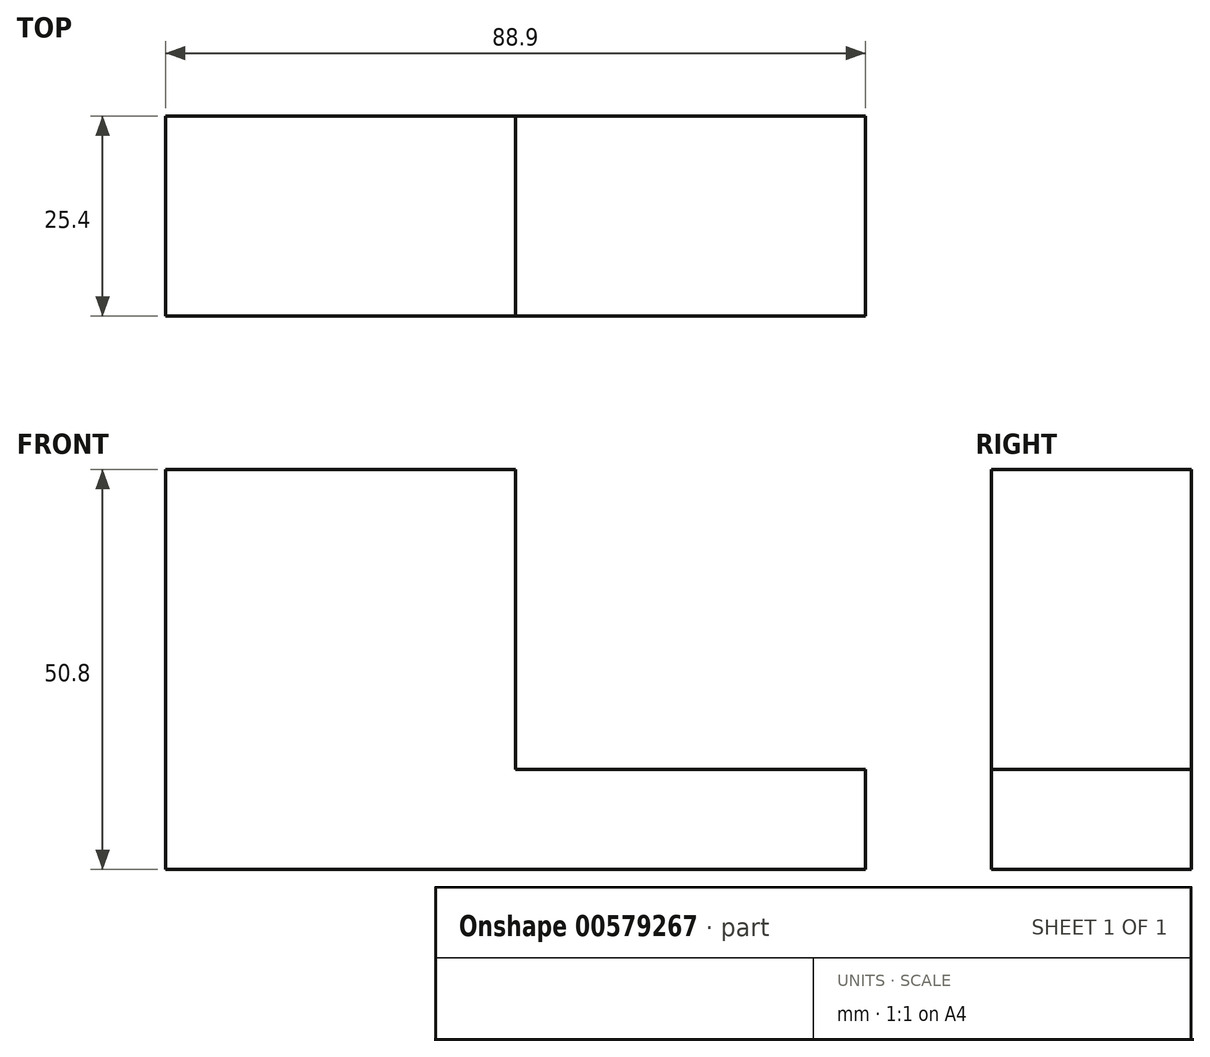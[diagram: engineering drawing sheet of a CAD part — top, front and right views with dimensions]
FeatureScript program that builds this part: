
annotation { "Feature Type Name" : "Feature", "Feature Type Description" : "" }
export const myFeature = defineFeature(function(context is Context, id is Id, definition is map)
    precondition{}
    {
        {
            var Q0;
            Q0=qCreatedBy(makeId("Front.planeOp"),FACE);
            var sketch = newSketch(context, id + "F0", { "sketchPlane" : qUnion([Q0])});
            skLineSegment(sketch, "E0", {"start": v(-48.67, 0) * mm, "end": v(40.23, 0) * mm});
            skLineSegment(sketch, "E1", {"start": v(40.23, 0) * mm, "end": v(40.23, 12.7) * mm});
            skLineSegment(sketch, "E2", {"start": v(40.23, 12.7) * mm, "end": v(-4.22, 12.7) * mm});
            skLineSegment(sketch, "E3", {"start": v(-4.22, 12.7) * mm, "end": v(-4.22, 50.8) * mm});
            skLineSegment(sketch, "E4", {"start": v(-4.22, 50.8) * mm, "end": v(-48.67, 50.8) * mm});
            skLineSegment(sketch, "E5", {"start": v(-48.67, 50.8) * mm, "end": v(-48.67, 0) * mm});
            skSolve(sketch);
        }
        {
            var Q0;
            Q0=makeQuery(id+"F0.imprint","IMPRINT",FACE,{"disambiguationData":[TD([[makeQuery(id+"F0.imprint","IMPRINT",EDGE,{"derivedFrom":sQuery(id+"F0.wireOp",EDGE,"E0")}),1.0]])]});
            extrude(context, id + "F1", {"entities" : qUnion([Q0]), "depth" : 25.4 * mm, "offsetDistance" : 25.4 * mm});
        }
        {
            var Q0;
            Q0=makeQuery(id+"F1.opExtrude","SWEPT_FACE",FACE,{"disambiguationData":[OSD([sQuery(id+"F0.wireOp",EDGE,"E2")])]});
            var sketch = newSketch(context, id + "F2", { "sketchPlane" : qUnion([Q0])});
            skSolve(sketch);
        }
    });
